# Revit family: Cleanout_Round_Floor-Zurn-Z1745
name_source: partatom
category: Plumbing Fixtures
units: mm (PartAtom-declared; Revit-internal decimal feet)

## family parameters
Always vertical = Yes
Cut with Voids When Loaded = No
Maintain Annotation Orientation = No
OmniClass Number = 23.45.55.21
OmniClass Title = Drains (Wastes)
Part Type = Normal
Room Calculation Point = No
Round Connector Dimension = Use Radius
Shared = No
Work Plane-Based = No

## types (18) — shared parameters
Assembly Code = D2030300
CW Connection = No
Default Elevation = 20 "
Description = FLOOR CLEANOUT WITH O-RING SEAL PLUG
HW Connection = No
Manufacturer = Zurn Water, LLC
Manufacurer Brand = Zurn
Modified Date = 01/09/2026
Product Documentation Link = https://files.zurn.com
Product Page URL = https://www.zurn.com
Product data url = https://www.bimobject.com
URL = www.zurn.com
Vent Connection = No
WFU = 1
Waste Connection = Yes
zero-valued in all types: CWFU, HWFU

## per-type parameters (varying)
| type | Approx. Weight (Lbs) | Body HT Dim 'E' | Butt Weld Angle | Dim "B" | Dim "C" | Main Material | Model | Pipe Size 'A' (Inner Diameter) | Pipe Size 'A' (Inner Radius) | Pipe Size 'A' (Nominal Diameter) | Pipe Size 'A' (Nominal Radius) | Pipe Size 'A' (Outer Diameter) | Pipe Size 'A' (Outer Radius) | Type Comments |
| Z1745-2BW | 6.00 lb | 1.625 " | 37.50° | 2.75 " | 4 " | Steel - Zurn - Stainless - Type - 304 | Z1745 | 2.067 " | 1.034 " | 2 " | 1 " | 2.375 " | 1.188 " | Z1745 - 2 Inch Butt-weld Outlet |
| Z1745-3BW | 6.00 lb | 1.625 " | 37.50° | 3.5 " | 4.875 " | Steel - Zurn - Stainless - Type - 304 | Z1745 | 3.068 " | 1.534 " | 3 " | 1.5 " | 3.5 " | 1.75 " | Z1745 - 3 Inch Butt-weld Outlet |
| Z1745-4BW | 6.00 lb | 1.625 " | 37.50° | 4.5 " | 6 " | Steel - Zurn - Stainless - Type - 304 | Z1745 | 4.026 " | 2.013 " | 4 " | 2 " | 4.5 " | 2.25 " | Z1745 - 4 Inch Butt-weld Outlet |
| Z1745-6BW | 10.00 lb | 1.625 " | 37.50° | 7.875 " | 9.375 " | Steel - Zurn - Stainless - Type - 304 | Z1745 | 6.065 " | 3.033 " | 6 " | 3 " | 6.625 " | 3.313 " | Z1745 - 6 Inch Butt-weld Outlet |
| Z1745-8BW | 10.00 lb | 2.5 " | 37.50° | 9.875 " | 11 " | Steel - Zurn - Stainless - Type - 304 | Z1745 | 7.981 " | 3.991 " | 8 " | 4 " | 8.625 " | 4.313 " | Z1745 - 8 Inch Butt-weld Outlet |
| Z1745-2IC | 6.00 lb | 3.375 " | 0.00° | 2.75 " | 4 " | Steel - Zurn - Stainless - Type - 304 | Z1745 | 2.067 " | 1.034 " | 2 " | 1 " | 2.375 " | 1.188 " | Z1745 - 2 Inch Inside Caulk Outlet |
| Z1745-3IC | 6.00 lb | 3.375 " | 0.00° | 3.5 " | 4.875 " | Steel - Zurn - Stainless - Type - 304 | Z1745 | 3.068 " | 1.534 " | 3 " | 1.5 " | 3.5 " | 1.75 " | Z1745 - 3 Inch Inside Caulk Outlet |
| Z1745-4IC | 6.00 lb | 3.375 " | 0.00° | 4.5 " | 6 " | Steel - Zurn - Stainless - Type - 304 | Z1745 | 4.026 " | 2.013 " | 4 " | 2 " | 4.5 " | 2.25 " | Z1745 - 4 Inch Inside Caulk Outlet |
| Z1745-6IC | 10.00 lb | 3.375 " | 0.00° | 7.875 " | 9.375 " | Steel - Zurn - Stainless - Type - 304 | Z1745 | 6.065 " | 3.033 " | 6 " | 3 " | 6.625 " | 3.313 " | Z1745 - 6 Inch Inside Caulk Outlet |
| ZM1745-2BW | 6.00 lb | 1.625 " | 37.50° | 2.75 " | 4 " | Steel - Zurn - Stainless - Type - 316 | ZM1745 | 2.067 " | 1.034 " | 2 " | 1 " | 2.375 " | 1.188 " | ZM1745 - 2 Inch Butt-weld Outlet |
| ZM1745-3BW | 6.00 lb | 1.625 " | 37.50° | 3.5 " | 4.875 " | Steel - Zurn - Stainless - Type - 316 | ZM1745 | 3.068 " | 1.534 " | 3 " | 1.5 " | 3.5 " | 1.75 " | ZM1745 - 3 Inch Butt-weld Outlet |
| ZM1745-4BW | 6.00 lb | 1.625 " | 37.50° | 4.5 " | 6 " | Steel - Zurn - Stainless - Type - 316 | ZM1745 | 4.026 " | 2.013 " | 4 " | 2 " | 4.5 " | 2.25 " | ZM1745 - 4 Inch Butt-weld Outlet |
| ZM1745-6BW | 10.00 lb | 1.625 " | 37.50° | 7.875 " | 9.375 " | Steel - Zurn - Stainless - Type - 316 | ZM1745 | 6.065 " | 3.033 " | 6 " | 3 " | 6.625 " | 3.313 " | ZM1745 - 6 Inch Butt-weld Outlet |
| ZM1745-8BW | 10.00 lb | 2.5 " | 37.50° | 9.875 " | 11 " | Steel - Zurn - Stainless - Type - 316 | ZM1745 | 7.981 " | 3.991 " | 8 " | 4 " | 8.625 " | 4.313 " | ZM1745 - 8 Inch Butt-weld Outlet |
| ZM1745-2IC | 6.00 lb | 3.375 " | 0.00° | 2.75 " | 4 " | Steel - Zurn - Stainless - Type - 316 | ZM1745 | 2.067 " | 1.034 " | 2 " | 1 " | 2.375 " | 1.188 " | ZM1745 - 2 Inch Inside Caulk Outlet |
| ZM1745-3IC | 6.00 lb | 3.375 " | 0.00° | 3.5 " | 4.875 " | Steel - Zurn - Stainless - Type - 316 | ZM1745 | 3.068 " | 1.534 " | 3 " | 1.5 " | 3.5 " | 1.75 " | ZM1745 - 3 Inch Inside Caulk Outlet |
| ZM1745-4IC | 6.00 lb | 3.375 " | 0.00° | 4.5 " | 6 " | Steel - Zurn - Stainless - Type - 316 | ZM1745 | 4.026 " | 2.013 " | 4 " | 2 " | 4.5 " | 2.25 " | ZM1745 - 4 Inch Inside Caulk Outlet |
| ZM1745-6IC | 10.00 lb | 3.375 " | 0.00° | 7.875 " | 9.375 " | Steel - Zurn - Stainless - Type - 316 | ZM1745 | 6.065 " | 3.033 " | 6 " | 3 " | 6.625 " | 3.313 " | ZM1745 - 6 Inch Inside Caulk Outlet |

## geometry (parser evidence)
native form markers: Blend x6, Sweep x2
no freeform markers — native parametric forms only
